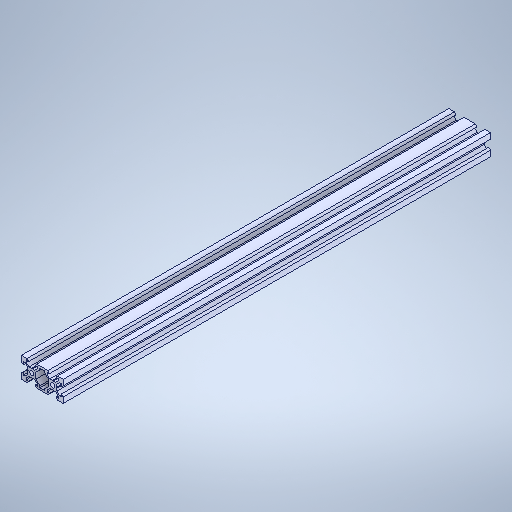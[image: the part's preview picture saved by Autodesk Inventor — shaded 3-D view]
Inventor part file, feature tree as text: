
AUTODESK INVENTOR PART (.ipt)
format: ipt  version: 2025.2 (Build 292293000, 293)  size: 358,400 bytes
history: native  units: in
note: dims shown in document units (in); Inventor stores cm internally (conversion verified against a paired STEP export)
features: extrude x1, sketch x1, other x1
ambient origin geometry x8: Origin, YZ Plane, XZ Plane, XY Plane, X Axis, Y Axis, Z Axis, Center Point
bodies: Solid1 (feature_tree)
feature tree (3):
  extrude  "Extrusion1"  [1 undecoded]
  sketch  "Sketch1"  dims[d0=3.5433in d1=0.0in]
  other  "Boss-Extrude1"
note: 1 required parameter value undecoded (feature->parameter linkage not recoverable at this tier; creation-order binding heuristic only, values carry confidence <= 0.55)
